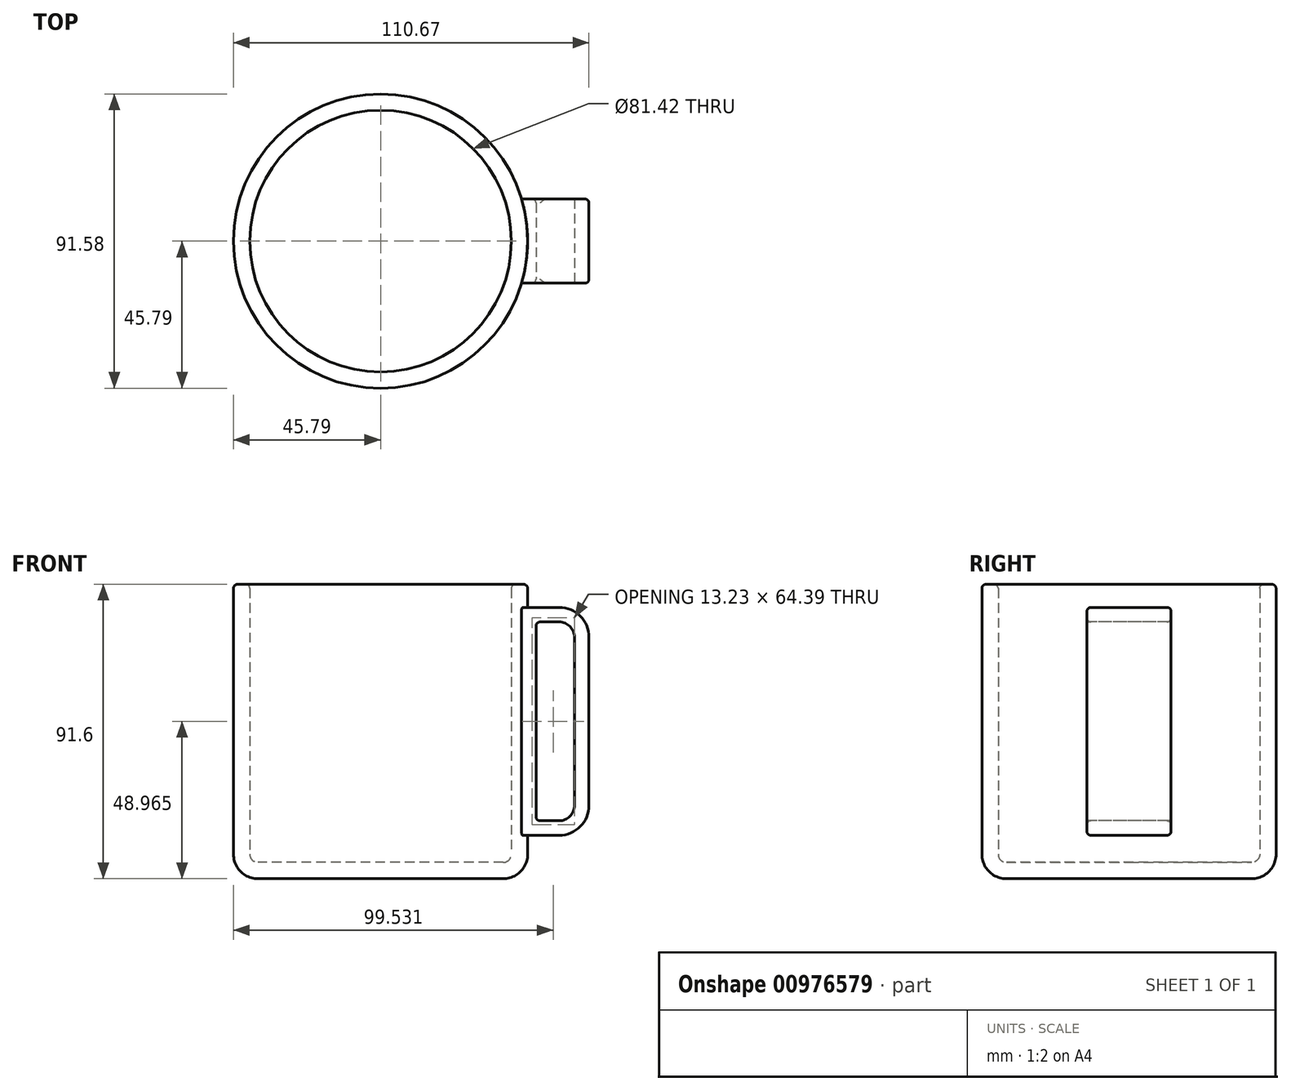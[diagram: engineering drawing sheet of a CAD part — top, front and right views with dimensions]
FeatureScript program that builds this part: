
annotation { "Feature Type Name" : "Feature", "Feature Type Description" : "" }
export const myFeature = defineFeature(function(context is Context, id is Id, definition is map)
    precondition{}
    {
        {
            var Q0;
            Q0=qCreatedBy(makeId("Top.planeOp"),FACE);
            var sketch = newSketch(context, id + "F0", { "sketchPlane" : qUnion([Q0])});
            skCircle(sketch, "E0", {"center": v(0, 0) * mm, "radius": 45.79 * mm});
            skSolve(sketch);
        }
        {
            var Q0;
            Q0=makeQuery(id+"F0.imprint","IMPRINT",FACE,{"disambiguationData":[TD([[makeQuery(id+"F0.imprint","IMPRINT",EDGE,{"derivedFrom":sQuery(id+"F0.wireOp",EDGE,"E0")}),1.0]])]});
            extrude(context, id + "F1", {"entities" : qUnion([Q0]), "depth" : 91.6 * mm, "offsetDistance" : 25.4 * mm});
        }
        {
            var Q0;
            Q0=makeQuery(id+"F1.opExtrude","CAP_FACE",FACE,{"disambiguationData":[OSD([sQuery(id+"F0.wireOp",EDGE,"E0")])],"isStart":true});
            fillet(context, id + "F2", {"entities" : qUnion([Q0]), "radius" : 7.62 * mm, "tangentPropagation" : true, "allowEdgeOverflow" : false});
        }
        {
            var Q0;
            Q0=makeQuery(id+"F1.opExtrude","CAP_FACE",FACE,{"disambiguationData":[OSD([sQuery(id+"F0.wireOp",EDGE,"E0")])],"isStart":false});
            shell(context, id + "F3", {"entities" : qUnion([Q0]), "thickness" : 5.08 * mm});
        }
        {
            var Q0;
            Q0=qCreatedBy(makeId("Right.planeOp"),FACE);
            cPlane(context, id + "F4", {"entities" : qUnion([Q0]), "cplaneType" : CPlaneType.OFFSET, "offset" : 64.88 * mm, "width" : 152.4 * mm, "height" : 152.4 * mm});
        }
        {
            var Q0;
            Q0=qCreatedBy(id+"F4.planeOp",FACE);
            var sketch = newSketch(context, id + "F5", { "sketchPlane" : qUnion([Q0])});
            skLineSegment(sketch, "E1.top", {"start": v(13.1, 41.08) * mm, "end": v(-13.1, 41.08) * mm});
            skLineSegment(sketch, "E1.left", {"start": v(13.1, 13.5) * mm, "end": v(13.1, 41.08) * mm});
            skLineSegment(sketch, "E1.right", {"start": v(-13.1, 13.5) * mm, "end": v(-13.1, 41.08) * mm});
            skPoint(sketch, "E1.middle", {"position": v(0, 0) * mm});
            skLineSegment(sketch, "E2.bottom", {"start": v(-13.1, 41.08) * mm, "end": v(13.1, 41.08) * mm, "construction": true});
            skLineSegment(sketch, "E2.top", {"start": v(-13.1, 13.5) * mm, "end": v(13.1, 13.5) * mm, "construction": true});
            skLineSegment(sketch, "E2.left", {"start": v(-13.1, 41.08) * mm, "end": v(-13.1, 13.5) * mm, "construction": true});
            skLineSegment(sketch, "E2.right", {"start": v(13.1, 41.08) * mm, "end": v(13.1, 13.5) * mm, "construction": true});
            skPoint(sketch, "E3.orphan", {"position": v(13.1, -41.08) * mm});
            skPoint(sketch, "E4.orphan", {"position": v(-13.1, -41.08) * mm});
            skPoint(sketch, "E5.oppositeSnap0", {"position": v(-13.1, 27.3) * mm});
            skLineSegment(sketch, "E5.bottom", {"start": v(13.1, 13.5) * mm, "end": v(-13.1, 13.5) * mm});
            skLineSegment(sketch, "E5.top", {"start": v(13.1, 84.42) * mm, "end": v(-13.1, 84.42) * mm});
            skLineSegment(sketch, "E5.left", {"start": v(13.1, 13.5) * mm, "end": v(13.1, 84.42) * mm});
            skLineSegment(sketch, "E5.right", {"start": v(-13.1, 13.5) * mm, "end": v(-13.1, 84.42) * mm});
            skSolve(sketch);
        }
        {
            var Q0;
            {var subQ0=sQuery(id+"F5.wireOp",EDGE,"E1.top");Q0=makeQuery(id+"F5.imprint","IMPRINT",FACE,{"disambiguationData":[TD([[makeQuery(id+"F5.imprint","IMPRINT",EDGE,{"derivedFrom":subQ0}),-1.0]])]});}
            var Q1;
            {var subQ0=sQuery(id+"F5.wireOp",EDGE,"E1.top");Q1=makeQuery(id+"F5.imprint","IMPRINT",FACE,{"disambiguationData":[TD([[makeQuery(id+"F5.imprint","IMPRINT",EDGE,{"derivedFrom":subQ0}),1.0]])]});}
            extrude(context, id + "F6", {"entities" : qUnion([Q0, Q1]), "operationType" : NewBodyOperationType.ADD, "endBound" : BoundingType.UP_TO_NEXT, "oppositeDirection" : true, "depth" : 25.4 * mm, "offsetDistance" : 25.4 * mm});
        }
        {
            var Q0;
            Q0=makeQuery(id+"F6.opExtrude","CAP_EDGE",EDGE,{"disambiguationData":[OSD([sQuery(id+"F5.wireOp",EDGE,"E5.top")])],"isStart":true});
            var Q1;
            Q1=makeQuery(id+"F6.opExtrude","CAP_EDGE",EDGE,{"disambiguationData":[OSD([sQuery(id+"F5.wireOp",EDGE,"E5.bottom")])],"isStart":true});
            fillet(context, id + "F7", {"entities" : qUnion([Q0, Q1]), "radius" : 9.32 * mm, "tangentPropagation" : true, "allowEdgeOverflow" : false});
        }
        {
            var Q0;
            Q0=makeQuery(id+"F6.opExtrude","SWEPT_FACE",FACE,{"disambiguationData":[OSD([sQuery(id+"F5.wireOp",EDGE,"E5.right")])]});
            var sketch = newSketch(context, id + "F8", { "sketchPlane" : qUnion([Q0])});
            skArc(sketch, "E6.0", {"start": v(55.56, 18.03) * mm, "mid": v(58.95, 19.44) * mm, "end": v(60.35, 22.83) * mm});
            skArc(sketch, "E6.1", {"start": v(60.35, 75.1) * mm, "mid": v(58.95, 78.5) * mm, "end": v(55.56, 79.9) * mm});
            skLineSegment(sketch, "E6.2", {"start": v(48.4, 79.9) * mm, "end": v(55.56, 79.9) * mm});
            skLineSegment(sketch, "E6.3", {"start": v(60.35, 22.83) * mm, "end": v(60.35, 75.1) * mm});
            skLineSegment(sketch, "E6.4", {"start": v(48.4, 18.03) * mm, "end": v(48.4, 79.9) * mm});
            skLineSegment(sketch, "E6.5", {"start": v(48.4, 18.03) * mm, "end": v(55.56, 18.03) * mm});
            skSolve(sketch);
        }
        {
            var Q0;
            Q0=makeQuery(id+"F8.imprint","IMPRINT",FACE,{"disambiguationData":[TD([[makeQuery(id+"F8.imprint","IMPRINT",EDGE,{"derivedFrom":sQuery(id+"F8.wireOp",EDGE,"E6.0")}),1.0]])]});
            extrude(context, id + "F9", {"entities" : qUnion([Q0]), "operationType" : NewBodyOperationType.REMOVE, "endBound" : BoundingType.UP_TO_NEXT, "oppositeDirection" : true, "depth" : 25.4 * mm, "offsetDistance" : 25.4 * mm});
        }
        {
            var Q0;
            Q0=makeQuery(id+"F1.opExtrude","CAP_EDGE",EDGE,{"disambiguationData":[OSD([sQuery(id+"F0.wireOp",EDGE,"E0")])],"isStart":false});
            var Q1;
            {var subQ0=sQuery(id+"F0.wireOp",EDGE,"E0");Q1=makeQuery(id+"F3.opShell","OFFSET_EDGE",EDGE,{"disambiguationData":[OSD([subQ0]),TDD([makeQuery(id+"F1.opExtrude","CAP_EDGE",EDGE,{"disambiguationData":[OSD([subQ0])],"isStart":false})])]});}
            var Q2;
            Q2=makeQuery(id+"F7.opFillet","BLEND_EDGE",EDGE,{"blendedFrom":[makeQuery(id+"F6.opExtrude","CAP_EDGE",EDGE,{"disambiguationData":[OSD([sQuery(id+"F5.wireOp",EDGE,"E5.top")])],"isStart":true}),makeQuery(id+"F6.opExtrude","SWEPT_FACE",FACE,{"disambiguationData":[OSD([sQuery(id+"F5.wireOp",EDGE,"E5.right")])]})],"blendedInto":[makeQuery(id+"F6.opExtrude","SWEPT_FACE",FACE,{"disambiguationData":[OSD([sQuery(id+"F5.wireOp",EDGE,"E5.right")])]})]});
            var Q3;
            Q3=makeQuery(id+"F6.opExtrude","SWEPT_EDGE",EDGE,{"disambiguationData":[OSD([sQuery(id+"F5.wireOp",EDGE,"E5.top"),sQuery(id+"F5.wireOp",EDGE,"E5.right")])]});
            var Q4;
            Q4=makeQuery(id+"F6.opExtrude","CAP_FACE",FACE,{"disambiguationData":[OSD([sQuery(id+"F5.wireOp",EDGE,"E5.bottom"),sQuery(id+"F5.wireOp",EDGE,"E5.top"),sQuery(id+"F5.wireOp",EDGE,"E5.left"),sQuery(id+"F5.wireOp",EDGE,"E5.right")])],"isStart":true});
            var Q5;
            Q5=makeQuery(id+"F9.boolean.opBoolean","COPY",FACE,{"derivedFrom":makeQuery(id+"F9.opExtrude","SWEPT_FACE",FACE,{"disambiguationData":[OSD([sQuery(id+"F8.wireOp",EDGE,"E6.4")])]})});
            var Q6;
            Q6=makeQuery(id+"F6.opExtrude","CAP_EDGE",EDGE,{"disambiguationData":[OSD([sQuery(id+"F5.wireOp",EDGE,"E5.right")])],"isStart":false});
            fillet(context, id + "F10", {"entities" : qUnion([Q0, Q1, Q2, Q3, Q4, Q5, Q6]), "radius" : 1.27 * mm, "tangentPropagation" : true, "allowEdgeOverflow" : false});
        }
    });
